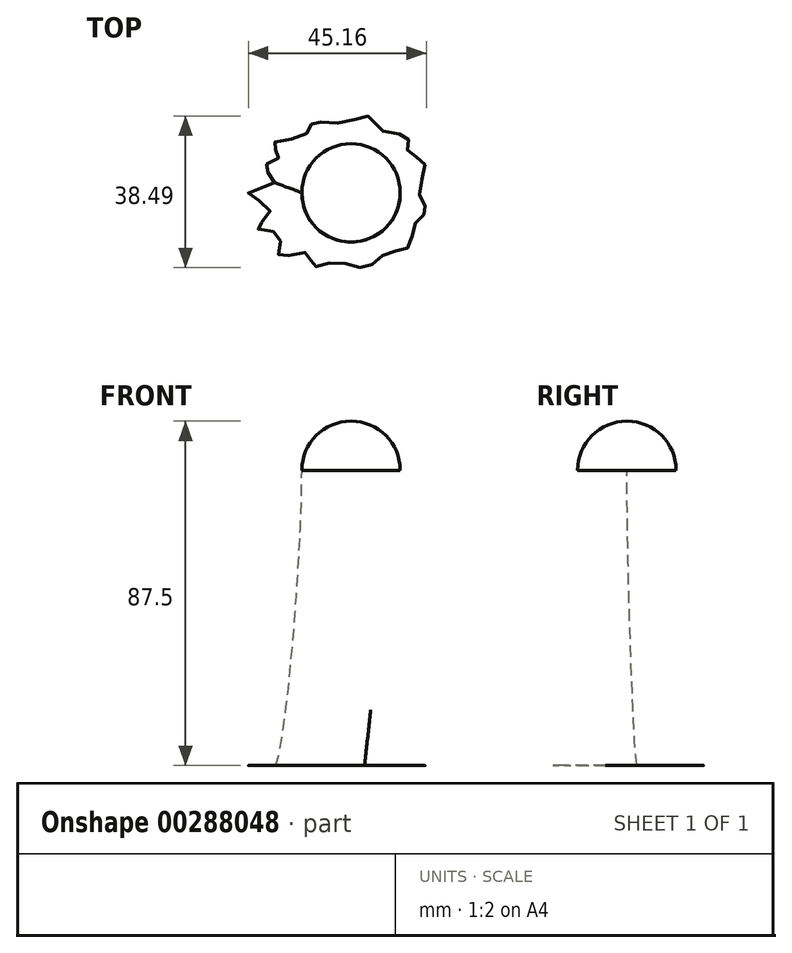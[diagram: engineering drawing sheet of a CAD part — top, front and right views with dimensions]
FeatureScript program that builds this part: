
annotation { "Feature Type Name" : "Feature", "Feature Type Description" : "" }
export const myFeature = defineFeature(function(context is Context, id is Id, definition is map)
    precondition{}
    {
        {
            var Q0;
            Q0=qCreatedBy(makeId("Top.planeOp"),FACE);
            var sketch = newSketch(context, id + "F0", { "sketchPlane" : qUnion([Q0])});
            skFitSpline(sketch, "E0", {"points": [v(-2.79, 17.74) * mm, v(4.84, 19.37) * mm, v(7.22, 16.12) * mm, v(14.35, 14.12) * mm, v(14.47, 10.5) * mm, v(18.6, 7.74) * mm, v(17.35, 0) * mm, v(19.1, -4.52) * mm, v(16.22, -7.9) * mm, v(14.6, -13.77) * mm, v(8.85, -15.4) * mm, v(3.84, -18.9) * mm, v(-3.91, -17.65) * mm, v(-9.66, -18.52) * mm, v(-11.16, -15.27) * mm, v(-18.3, -16.02) * mm, v(-18.17, -10.77) * mm, v(-23.92, -8.9) * mm, v(-20.54, -4.52) * mm, v(-26.05, 0) * mm, v(-19.42, 2.61) * mm, v(-22.05, 6.61) * mm, v(-18.17, 9.24) * mm, v(-19.92, 12.37) * mm, v(-11.92, 14.62) * mm, v(-9.66, 17.74) * mm, v(-2.79, 17.74) * mm]});
            skSolve(sketch);
        }
        {
            var Q0;
            Q0=qCreatedBy(makeId("Top.planeOp"),FACE);
            cPlane(context, id + "F1", {"entities" : qUnion([Q0]), "cplaneType" : CPlaneType.OFFSET, "offset" : 75 * mm, "width" : 150 * mm, "height" : 150 * mm});
        }
        {
            var Q0;
            Q0=qCreatedBy(id+"F1.planeOp",FACE);
            var sketch = newSketch(context, id + "F2", { "sketchPlane" : qUnion([Q0])});
            skCircle(sketch, "E1", {"center": v(0, 0) * mm, "radius": 12.5 * mm});
            skLineSegment(sketch, "E2", {"start": v(-12.5, 0) * mm, "end": v(12.5, 0) * mm});
            skSolve(sketch);
        }
        {
            var Q0;
            Q0=qCreatedBy(makeId("Front.planeOp"),FACE);
            var sketch = newSketch(context, id + "F3", { "sketchPlane" : qUnion([Q0])});
            skLineSegment(sketch, "E3.0", {"start": v(-12.5, 75) * mm, "end": v(12.5, 75) * mm});
            skPoint(sketch, "E4.0", {"position": v(17.35, 0) * mm});
            skPoint(sketch, "E5.0", {"position": v(-26.05, 0) * mm});
            skFitSpline(sketch, "E6", {"points": [v(-12.5, 75) * mm, v(-26.05, 0) * mm], "startDerivative": vector(0, -102.77) * mm, "endDerivative": vector(-30.96, -77.05) * mm});
            skFitSpline(sketch, "E7", {"points": [v(12.5, 75) * mm, v(17.35, 0) * mm], "startDerivative": vector(0, -16.34) * mm, "endDerivative": vector(-7.71, -95.04) * mm});
            skSolve(sketch);
        }
        {
            var Q0;
            {var subQ0=sQuery(id+"F2.wireOp",EDGE,"E2");Q0=makeQuery(id+"F2.imprint","IMPRINT",FACE,{"disambiguationData":[TD([[makeQuery(id+"F2.imprint","IMPRINT",EDGE,{"derivedFrom":subQ0}),1.0]])]});}
            var Q1;
            Q1=sQuery(id+"F2.wireOp",EDGE,"E2");
            revolve(context, id + "F4", {"entities" : qUnion([Q0]), "axis" : qUnion([Q1]), "revolveType" : RevolveType.ONE_DIRECTION, "angle" : 180 * degree});
        }
        {
            var Q1;
            Q1=makeQuery(id+"F0.imprint","IMPRINT",FACE,{"disambiguationData":[TD([[makeQuery(id+"F0.imprint","IMPRINT",EDGE,{"derivedFrom":sQuery(id+"F0.wireOp",EDGE,"E0")}),-1.0]])]});
            var Q2;
            Q2=makeQuery(id+"F2.imprint","IMPRINT",FACE,{"disambiguationData":[TD([[makeQuery(id+"F2.imprint","IMPRINT",EDGE,{"derivedFrom":sQuery(id+"F2.wireOp",EDGE,"E1")}),1.0]])]});
            var Q3;
            Q3=sQuery(id+"F3.wireOp",EDGE,"E6");
            var Q4;
            Q4=sQuery(id+"F3.wireOp",EDGE,"E7");
            loft(context, id + "F5", {"operationType" : NewBodyOperationType.ADD, "startCondition" : LoftEndDerivativeType.TANGENT_TO_PROFILE, "startMagnitude" : 1, "endCondition" : LoftEndDerivativeType.NORMAL_TO_PROFILE, "endMagnitude" : 1, "sheetProfilesArray" : [{ "sheetProfileEntities" : qUnion([Q1]) }, { "sheetProfileEntities" : qUnion([Q2]) }], "guidesArray" : [{ "guideEntities" : qUnion([Q3]), "guideDerivativeType" : LoftGuideDerivativeType.DEFAULT, "guideDerivativeMagnitude" : 1 }, { "guideEntities" : qUnion([Q4]), "guideDerivativeType" : LoftGuideDerivativeType.DEFAULT, "guideDerivativeMagnitude" : 1 }]});
        }
    });
